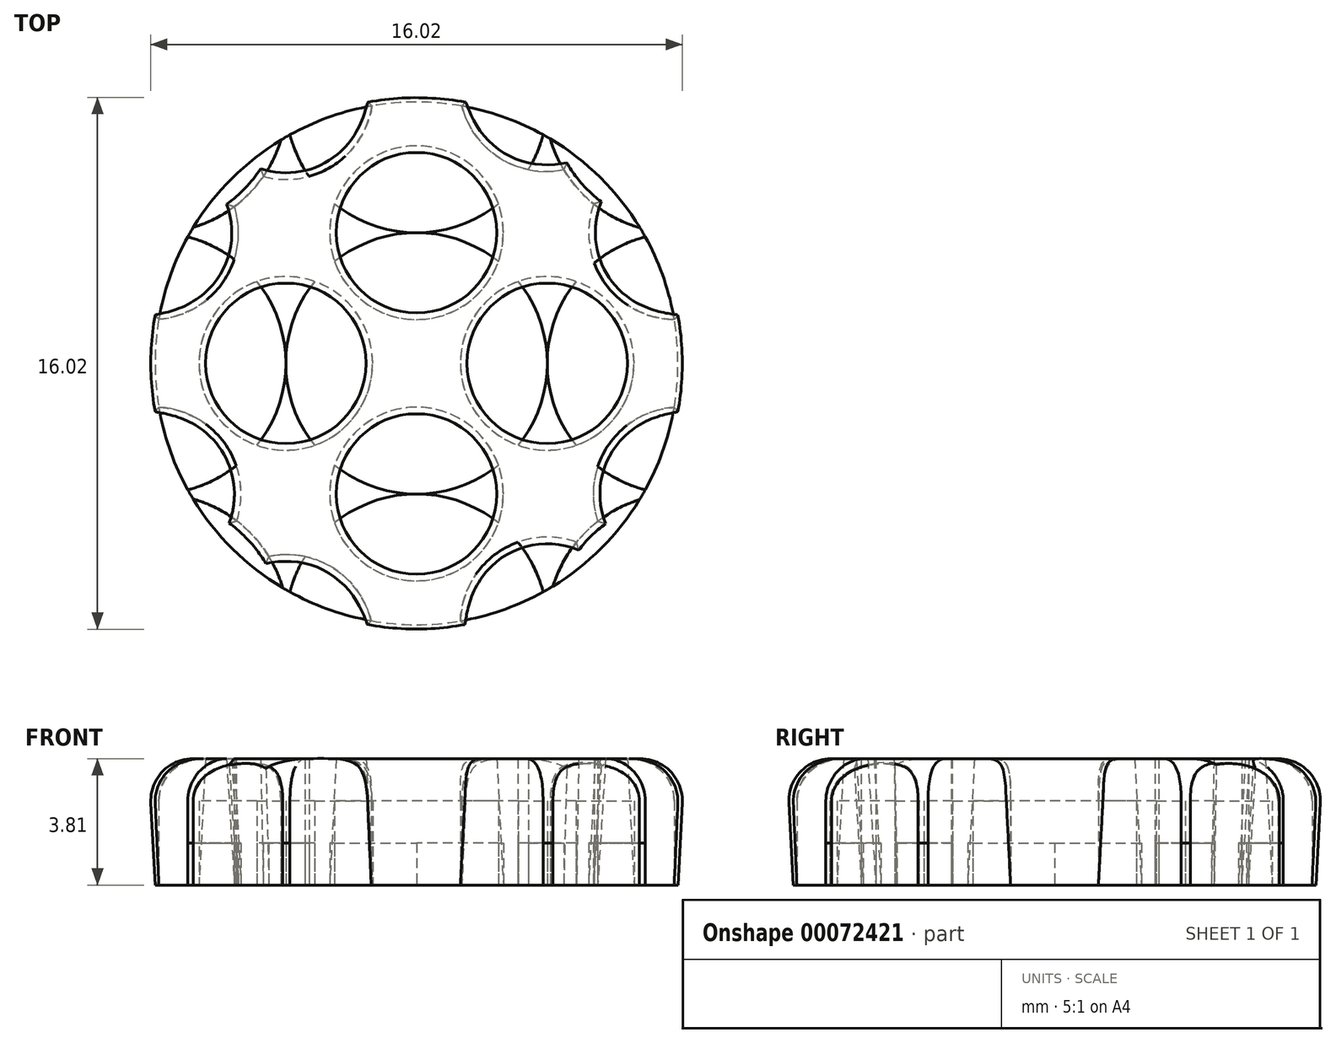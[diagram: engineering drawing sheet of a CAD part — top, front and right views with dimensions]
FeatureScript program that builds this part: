
annotation { "Feature Type Name" : "Feature", "Feature Type Description" : "" }
export const myFeature = defineFeature(function(context is Context, id is Id, definition is map)
    precondition{}
    {
        {
            var Q0;
            Q0=qCreatedBy(makeId("Top.planeOp"),FACE);
            var sketch = newSketch(context, id + "F0", { "sketchPlane" : qUnion([Q0])});
            skCircle(sketch, "E0", {"center": v(0, 0) * mm, "radius": 7.87 * mm});
            skCircle(sketch, "E1", {"center": v(0, 0) * mm, "radius": 3.94 * mm});
            skCircle(sketch, "E2", {"center": v(3.94, 0) * mm, "radius": 2.62 * mm});
            skCircle(sketch, "E3", {"center": v(-3.94, 0) * mm, "radius": 2.62 * mm});
            skCircle(sketch, "E4", {"center": v(0, 3.94) * mm, "radius": 2.62 * mm});
            skCircle(sketch, "E5", {"center": v(0, -3.94) * mm, "radius": 2.62 * mm});
            skCircle(sketch, "E6", {"center": v(-7.87, 0) * mm, "radius": 3.94 * mm});
            skCircle(sketch, "E7", {"center": v(7.87, 0) * mm, "radius": 3.94 * mm});
            skCircle(sketch, "E8", {"center": v(0, 7.87) * mm, "radius": 3.94 * mm});
            skCircle(sketch, "E9", {"center": v(0, -7.87) * mm, "radius": 3.94 * mm});
            skCircle(sketch, "E10", {"center": v(-7.85, 7.87) * mm, "radius": 3.94 * mm});
            skPoint(sketch, "E10.first.point", {"position": v(-3.93, 8.16) * mm});
            skPoint(sketch, "E10.second.point", {"position": v(-11.67, 8.83) * mm});
            skPoint(sketch, "E10.third.point", {"position": v(-7.98, 3.94) * mm});
            skCircle(sketch, "E11", {"center": v(7.8, 7.87) * mm, "radius": 3.94 * mm});
            skPoint(sketch, "E11.first.point", {"position": v(3.9, 8.4) * mm});
            skPoint(sketch, "E11.second.point", {"position": v(11.72, 8.27) * mm});
            skPoint(sketch, "E11.third.point", {"position": v(7.8, 3.94) * mm});
            skCircle(sketch, "E12", {"center": v(7.87, -7.87) * mm, "radius": 3.94 * mm});
            skPoint(sketch, "E12.first.point", {"position": v(7.94, -3.94) * mm});
            skPoint(sketch, "E12.second.point", {"position": v(7.53, -11.8) * mm});
            skPoint(sketch, "E12.third.point", {"position": v(3.94, -7.85) * mm});
            skCircle(sketch, "E13", {"center": v(-7.8, -7.87) * mm, "radius": 3.94 * mm});
            skPoint(sketch, "E13.first.point", {"position": v(-7.9, -3.94) * mm});
            skPoint(sketch, "E13.second.point", {"position": v(-9.84, -11.24) * mm});
            skPoint(sketch, "E13.third.point", {"position": v(-3.9, -8.38) * mm});
            skCircle(sketch, "E14", {"center": v(-3.9, -8.38) * mm, "radius": 2.62 * mm});
            skCircle(sketch, "E15", {"center": v(3.94, -7.85) * mm, "radius": 2.62 * mm});
            skCircle(sketch, "E16", {"center": v(7.8, 3.94) * mm, "radius": 2.62 * mm});
            skCircle(sketch, "E17", {"center": v(7.94, -3.94) * mm, "radius": 2.62 * mm});
            skCircle(sketch, "E18", {"center": v(-7.9, -3.94) * mm, "radius": 2.62 * mm});
            skCircle(sketch, "E19", {"center": v(3.9, 8.4) * mm, "radius": 2.62 * mm});
            skCircle(sketch, "E20", {"center": v(-7.98, 3.94) * mm, "radius": 2.62 * mm});
            skCircle(sketch, "E21", {"center": v(-3.93, 8.16) * mm, "radius": 2.62 * mm});
            skSolve(sketch);
        }
        {
            var Q0;
            {var subQ0=sQuery(id+"F0.wireOp",EDGE,"E13");var subQ1=sQuery(id+"F0.wireOp",EDGE,"E0");var subQ2=makeQuery(id+"F0.imprint","INTERSECT",VERTEX,{"disambiguationData":[OD(1.0)],"derivedFrom":[subQ1,subQ0]});Q0=makeQuery(id+"F0.imprint","IMPRINT",FACE,{"disambiguationData":[TD([[makeQuery(id+"F0.imprint","IMPRINT",EDGE,{"disambiguationData":[TD([[subQ2,-1.0]])],"derivedFrom":subQ1}),1.0]])]});}
            var Q1;
            {var subQ0=sQuery(id+"F0.wireOp",EDGE,"E8");var subQ1=sQuery(id+"F0.wireOp",EDGE,"E1");var subQ2=makeQuery(id+"F0.imprint","INTERSECT",VERTEX,{"derivedFrom":[subQ1,subQ0]});Q1=makeQuery(id+"F0.imprint","IMPRINT",FACE,{"disambiguationData":[TD([[makeQuery(id+"F0.imprint","IMPRINT",EDGE,{"disambiguationData":[TD([[subQ2,-1.0]])],"derivedFrom":subQ1}),-1.0]])]});}
            var Q2;
            {var subQ0=sQuery(id+"F0.wireOp",EDGE,"E8");var subQ1=sQuery(id+"F0.wireOp",EDGE,"E0");var subQ2=makeQuery(id+"F0.imprint","INTERSECT",VERTEX,{"disambiguationData":[OD(1.0)],"derivedFrom":[subQ1,subQ0]});Q2=makeQuery(id+"F0.imprint","IMPRINT",FACE,{"disambiguationData":[TD([[makeQuery(id+"F0.imprint","IMPRINT",EDGE,{"disambiguationData":[TD([[subQ2,-1.0]])],"derivedFrom":subQ1}),1.0]])]});}
            var Q3;
            {var subQ0=sQuery(id+"F0.wireOp",EDGE,"E10");var subQ1=sQuery(id+"F0.wireOp",EDGE,"E0");var subQ2=makeQuery(id+"F0.imprint","INTERSECT",VERTEX,{"disambiguationData":[OD(1.0)],"derivedFrom":[subQ1,subQ0]});Q3=makeQuery(id+"F0.imprint","IMPRINT",FACE,{"disambiguationData":[TD([[makeQuery(id+"F0.imprint","IMPRINT",EDGE,{"disambiguationData":[TD([[subQ2,-1.0]])],"derivedFrom":subQ1}),1.0]])]});}
            var Q4;
            {var subQ0=sQuery(id+"F0.wireOp",EDGE,"E2");var subQ1=sQuery(id+"F0.wireOp",EDGE,"E1");var subQ2=makeQuery(id+"F0.imprint","INTERSECT",VERTEX,{"disambiguationData":[OD(0.0)],"derivedFrom":[subQ1,subQ0]});Q4=makeQuery(id+"F0.imprint","IMPRINT",FACE,{"disambiguationData":[TD([[makeQuery(id+"F0.imprint","IMPRINT",EDGE,{"disambiguationData":[TD([[subQ2,1.0]])],"derivedFrom":subQ1}),-1.0]])]});}
            var Q5;
            {var subQ0=sQuery(id+"F0.wireOp",EDGE,"E4");var subQ1=sQuery(id+"F0.wireOp",EDGE,"E1");var subQ2=makeQuery(id+"F0.imprint","INTERSECT",VERTEX,{"disambiguationData":[OD(0.0)],"derivedFrom":[subQ1,subQ0]});Q5=makeQuery(id+"F0.imprint","IMPRINT",FACE,{"disambiguationData":[TD([[makeQuery(id+"F0.imprint","IMPRINT",EDGE,{"disambiguationData":[TD([[subQ2,-1.0]])],"derivedFrom":subQ1}),-1.0]])]});}
            var Q6;
            {var subQ0=sQuery(id+"F0.wireOp",EDGE,"E7");var subQ1=sQuery(id+"F0.wireOp",EDGE,"E1");var subQ2=makeQuery(id+"F0.imprint","INTERSECT",VERTEX,{"derivedFrom":[subQ1,subQ0]});Q6=makeQuery(id+"F0.imprint","IMPRINT",FACE,{"disambiguationData":[TD([[makeQuery(id+"F0.imprint","IMPRINT",EDGE,{"disambiguationData":[TD([[subQ2,1.0]])],"derivedFrom":subQ1}),-1.0]])]});}
            var Q7;
            {var subQ0=sQuery(id+"F0.wireOp",EDGE,"E6");var subQ1=sQuery(id+"F0.wireOp",EDGE,"E0");var subQ2=makeQuery(id+"F0.imprint","INTERSECT",VERTEX,{"disambiguationData":[OD(1.0)],"derivedFrom":[subQ1,subQ0]});Q7=makeQuery(id+"F0.imprint","IMPRINT",FACE,{"disambiguationData":[TD([[makeQuery(id+"F0.imprint","IMPRINT",EDGE,{"disambiguationData":[TD([[subQ2,-1.0]])],"derivedFrom":subQ1}),1.0]])]});}
            var Q8;
            {var subQ0=sQuery(id+"F0.wireOp",EDGE,"E6");var subQ1=sQuery(id+"F0.wireOp",EDGE,"E1");var subQ2=makeQuery(id+"F0.imprint","INTERSECT",VERTEX,{"derivedFrom":[subQ1,subQ0]});Q8=makeQuery(id+"F0.imprint","IMPRINT",FACE,{"disambiguationData":[TD([[makeQuery(id+"F0.imprint","IMPRINT",EDGE,{"disambiguationData":[TD([[subQ2,-1.0]])],"derivedFrom":subQ1}),-1.0]])]});}
            var Q9;
            {var subQ0=sQuery(id+"F0.wireOp",EDGE,"E7");var subQ1=sQuery(id+"F0.wireOp",EDGE,"E0");var subQ2=makeQuery(id+"F0.imprint","INTERSECT",VERTEX,{"disambiguationData":[OD(0.0)],"derivedFrom":[subQ1,subQ0]});Q9=makeQuery(id+"F0.imprint","IMPRINT",FACE,{"disambiguationData":[TD([[makeQuery(id+"F0.imprint","IMPRINT",EDGE,{"disambiguationData":[TD([[subQ2,-1.0]])],"derivedFrom":subQ1}),1.0]])]});}
            var Q10;
            {var subQ0=sQuery(id+"F0.wireOp",EDGE,"E5");var subQ1=sQuery(id+"F0.wireOp",EDGE,"E1");var subQ2=makeQuery(id+"F0.imprint","INTERSECT",VERTEX,{"disambiguationData":[OD(0.0)],"derivedFrom":[subQ1,subQ0]});Q10=makeQuery(id+"F0.imprint","IMPRINT",FACE,{"disambiguationData":[TD([[makeQuery(id+"F0.imprint","IMPRINT",EDGE,{"disambiguationData":[TD([[subQ2,-1.0]])],"derivedFrom":subQ1}),-1.0]])]});}
            var Q11;
            {var subQ0=sQuery(id+"F0.wireOp",EDGE,"E12");var subQ1=sQuery(id+"F0.wireOp",EDGE,"E0");var subQ2=makeQuery(id+"F0.imprint","INTERSECT",VERTEX,{"disambiguationData":[OD(1.0)],"derivedFrom":[subQ1,subQ0]});Q11=makeQuery(id+"F0.imprint","IMPRINT",FACE,{"disambiguationData":[TD([[makeQuery(id+"F0.imprint","IMPRINT",EDGE,{"disambiguationData":[TD([[subQ2,-1.0]])],"derivedFrom":subQ1}),1.0]])]});}
            var Q12;
            {var subQ0=sQuery(id+"F0.wireOp",EDGE,"E3");var subQ1=sQuery(id+"F0.wireOp",EDGE,"E1");var subQ2=makeQuery(id+"F0.imprint","INTERSECT",VERTEX,{"disambiguationData":[OD(0.0)],"derivedFrom":[subQ1,subQ0]});Q12=makeQuery(id+"F0.imprint","IMPRINT",FACE,{"disambiguationData":[TD([[makeQuery(id+"F0.imprint","IMPRINT",EDGE,{"disambiguationData":[TD([[subQ2,-1.0]])],"derivedFrom":subQ1}),-1.0]])]});}
            var Q13;
            {var subQ0=sQuery(id+"F0.wireOp",EDGE,"E11");var subQ1=sQuery(id+"F0.wireOp",EDGE,"E0");var subQ2=makeQuery(id+"F0.imprint","INTERSECT",VERTEX,{"disambiguationData":[OD(1.0)],"derivedFrom":[subQ1,subQ0]});Q13=makeQuery(id+"F0.imprint","IMPRINT",FACE,{"disambiguationData":[TD([[makeQuery(id+"F0.imprint","IMPRINT",EDGE,{"disambiguationData":[TD([[subQ2,-1.0]])],"derivedFrom":subQ1}),1.0]])]});}
            var Q14;
            {var subQ0=sQuery(id+"F0.wireOp",EDGE,"E9");var subQ1=sQuery(id+"F0.wireOp",EDGE,"E1");var subQ2=makeQuery(id+"F0.imprint","INTERSECT",VERTEX,{"derivedFrom":[subQ1,subQ0]});Q14=makeQuery(id+"F0.imprint","IMPRINT",FACE,{"disambiguationData":[TD([[makeQuery(id+"F0.imprint","IMPRINT",EDGE,{"disambiguationData":[TD([[subQ2,-1.0]])],"derivedFrom":subQ1}),-1.0]])]});}
            var Q15;
            {var subQ0=sQuery(id+"F0.wireOp",EDGE,"E9");var subQ1=sQuery(id+"F0.wireOp",EDGE,"E0");var subQ2=makeQuery(id+"F0.imprint","INTERSECT",VERTEX,{"disambiguationData":[OD(1.0)],"derivedFrom":[subQ1,subQ0]});Q15=makeQuery(id+"F0.imprint","IMPRINT",FACE,{"disambiguationData":[TD([[makeQuery(id+"F0.imprint","IMPRINT",EDGE,{"disambiguationData":[TD([[subQ2,-1.0]])],"derivedFrom":subQ1}),1.0]])]});}
            extrude(context, id + "F1", {"entities" : qUnion([Q0, Q1, Q2, Q3, Q4, Q5, Q6, Q7, Q8, Q9, Q10, Q11, Q12, Q13, Q14, Q15]), "depth" : 1.27 * mm});
        }
        {
            var Q0;
            {var subQ9=sQuery(id+"F0.wireOp",EDGE,"E1");var subQ11=sQuery(id+"F0.wireOp",EDGE,"E5");var subQ12=makeQuery(id+"F0.imprint","INTERSECT",VERTEX,{"disambiguationData":[OD(1.0)],"derivedFrom":[subQ9,subQ11]});Q0=makeQuery(id+"F0.imprint","IMPRINT",FACE,{"disambiguationData":[TD([[makeQuery(id+"F0.imprint","IMPRINT",EDGE,{"disambiguationData":[TD([[subQ12,-1.0]])],"derivedFrom":subQ9}),-1.0]])]});}
            var Q1;
            {var subQ3=sQuery(id+"F0.wireOp",EDGE,"E19");var subQ8=sQuery(id+"F0.wireOp",EDGE,"E0");var subQ9=makeQuery(id+"F0.imprint","INTERSECT",VERTEX,{"disambiguationData":[OD(1.0)],"derivedFrom":[subQ8,subQ3]});Q1=makeQuery(id+"F0.imprint","IMPRINT",FACE,{"disambiguationData":[TD([[makeQuery(id+"F0.imprint","IMPRINT",EDGE,{"disambiguationData":[TD([[subQ9,-1.0]])],"derivedFrom":subQ8}),1.0]])]});}
            var Q2;
            {var subQ3=sQuery(id+"F0.wireOp",EDGE,"E14");var subQ6=sQuery(id+"F0.wireOp",EDGE,"E0");var subQ10=makeQuery(id+"F0.imprint","INTERSECT",VERTEX,{"disambiguationData":[OD(1.0)],"derivedFrom":[subQ6,subQ3]});Q2=makeQuery(id+"F0.imprint","IMPRINT",FACE,{"disambiguationData":[TD([[makeQuery(id+"F0.imprint","IMPRINT",EDGE,{"disambiguationData":[TD([[subQ10,-1.0]])],"derivedFrom":subQ6}),1.0]])]});}
            var Q3;
            {var subQ1=sQuery(id+"F0.wireOp",EDGE,"E1");var subQ5=sQuery(id+"F0.wireOp",EDGE,"E3");var subQ6=makeQuery(id+"F0.imprint","INTERSECT",VERTEX,{"disambiguationData":[OD(1.0)],"derivedFrom":[subQ1,subQ5]});Q3=makeQuery(id+"F0.imprint","IMPRINT",FACE,{"disambiguationData":[TD([[makeQuery(id+"F0.imprint","IMPRINT",EDGE,{"disambiguationData":[TD([[subQ6,-1.0]])],"derivedFrom":subQ1}),-1.0]])]});}
            var Q4;
            {var subQ6=sQuery(id+"F0.wireOp",EDGE,"E20");var subQ7=sQuery(id+"F0.wireOp",EDGE,"E0");var subQ8=makeQuery(id+"F0.imprint","INTERSECT",VERTEX,{"disambiguationData":[OD(1.0)],"derivedFrom":[subQ7,subQ6]});Q4=makeQuery(id+"F0.imprint","IMPRINT",FACE,{"disambiguationData":[TD([[makeQuery(id+"F0.imprint","IMPRINT",EDGE,{"disambiguationData":[TD([[subQ8,-1.0]])],"derivedFrom":subQ7}),1.0]])]});}
            var Q5;
            {var subQ1=sQuery(id+"F0.wireOp",EDGE,"E1");var subQ3=sQuery(id+"F0.wireOp",EDGE,"E2");var subQ11=makeQuery(id+"F0.imprint","INTERSECT",VERTEX,{"disambiguationData":[OD(0.0)],"derivedFrom":[subQ1,subQ3]});Q5=makeQuery(id+"F0.imprint","IMPRINT",FACE,{"disambiguationData":[TD([[makeQuery(id+"F0.imprint","IMPRINT",EDGE,{"disambiguationData":[TD([[subQ11,-1.0]])],"derivedFrom":subQ1}),1.0]])]});}
            var Q6;
            {var subQ6=sQuery(id+"F0.wireOp",EDGE,"E16");var subQ8=sQuery(id+"F0.wireOp",EDGE,"E0");var subQ9=makeQuery(id+"F0.imprint","INTERSECT",VERTEX,{"disambiguationData":[OD(0.0)],"derivedFrom":[subQ8,subQ6]});Q6=makeQuery(id+"F0.imprint","IMPRINT",FACE,{"disambiguationData":[TD([[makeQuery(id+"F0.imprint","IMPRINT",EDGE,{"disambiguationData":[TD([[subQ9,1.0]])],"derivedFrom":subQ8}),1.0]])]});}
            var Q7;
            {var subQ5=sQuery(id+"F0.wireOp",EDGE,"E4");var subQ6=sQuery(id+"F0.wireOp",EDGE,"E1");var subQ7=makeQuery(id+"F0.imprint","INTERSECT",VERTEX,{"disambiguationData":[OD(1.0)],"derivedFrom":[subQ6,subQ5]});Q7=makeQuery(id+"F0.imprint","IMPRINT",FACE,{"disambiguationData":[TD([[makeQuery(id+"F0.imprint","IMPRINT",EDGE,{"disambiguationData":[TD([[subQ7,-1.0]])],"derivedFrom":subQ6}),-1.0]])]});}
            var Q8;
            {var subQ1=sQuery(id+"F0.wireOp",EDGE,"E2");var subQ5=sQuery(id+"F0.wireOp",EDGE,"E1");var subQ6=makeQuery(id+"F0.imprint","INTERSECT",VERTEX,{"disambiguationData":[OD(0.0)],"derivedFrom":[subQ5,subQ1]});Q8=makeQuery(id+"F0.imprint","IMPRINT",FACE,{"disambiguationData":[TD([[makeQuery(id+"F0.imprint","IMPRINT",EDGE,{"disambiguationData":[TD([[subQ6,-1.0]])],"derivedFrom":subQ5}),-1.0]])]});}
            extrude(context, id + "F2", {"entities" : qUnion([Q0, Q1, Q2, Q3, Q4, Q5, Q6, Q7, Q8]), "depth" : 3.8 * mm, "hasDraft" : true, "draftAngle" : 3 * degree});
        }
        {
            var Q0;
            {var subQ0=sQuery(id+"F0.wireOp",EDGE,"E2");var subQ1=sQuery(id+"F0.wireOp",EDGE,"E1");var subQ2=makeQuery(id+"F0.imprint","INTERSECT",VERTEX,{"disambiguationData":[OD(0.0)],"derivedFrom":[subQ1,subQ0]});Q0=makeQuery(id+"F0.imprint","IMPRINT",FACE,{"disambiguationData":[TD([[makeQuery(id+"F0.imprint","IMPRINT",EDGE,{"disambiguationData":[TD([[subQ2,1.0]])],"derivedFrom":subQ1}),1.0]])]});}
            var Q1;
            {var subQ0=sQuery(id+"F0.wireOp",EDGE,"E5");var subQ1=sQuery(id+"F0.wireOp",EDGE,"E1");var subQ2=makeQuery(id+"F0.imprint","INTERSECT",VERTEX,{"disambiguationData":[OD(0.0)],"derivedFrom":[subQ1,subQ0]});Q1=makeQuery(id+"F0.imprint","IMPRINT",FACE,{"disambiguationData":[TD([[makeQuery(id+"F0.imprint","IMPRINT",EDGE,{"disambiguationData":[TD([[subQ2,-1.0]])],"derivedFrom":subQ1}),1.0]])]});}
            var Q2;
            {var subQ0=sQuery(id+"F0.wireOp",EDGE,"E4");var subQ1=sQuery(id+"F0.wireOp",EDGE,"E1");var subQ2=makeQuery(id+"F0.imprint","INTERSECT",VERTEX,{"disambiguationData":[OD(0.0)],"derivedFrom":[subQ1,subQ0]});Q2=makeQuery(id+"F0.imprint","IMPRINT",FACE,{"disambiguationData":[TD([[makeQuery(id+"F0.imprint","IMPRINT",EDGE,{"disambiguationData":[TD([[subQ2,-1.0]])],"derivedFrom":subQ1}),1.0]])]});}
            var Q3;
            {var subQ0=sQuery(id+"F0.wireOp",EDGE,"E8");var subQ1=sQuery(id+"F0.wireOp",EDGE,"E4");var subQ2=makeQuery(id+"F0.imprint","INTERSECT",VERTEX,{"disambiguationData":[OD(0.0)],"derivedFrom":[subQ1,subQ0]});Q3=makeQuery(id+"F0.imprint","IMPRINT",FACE,{"disambiguationData":[TD([[makeQuery(id+"F0.imprint","IMPRINT",EDGE,{"disambiguationData":[TD([[subQ2,1.0]])],"derivedFrom":subQ1}),1.0]])]});}
            var Q4;
            {var subQ0=sQuery(id+"F0.wireOp",EDGE,"E6");var subQ1=sQuery(id+"F0.wireOp",EDGE,"E3");var subQ2=makeQuery(id+"F0.imprint","INTERSECT",VERTEX,{"disambiguationData":[OD(0.0)],"derivedFrom":[subQ1,subQ0]});Q4=makeQuery(id+"F0.imprint","IMPRINT",FACE,{"disambiguationData":[TD([[makeQuery(id+"F0.imprint","IMPRINT",EDGE,{"disambiguationData":[TD([[subQ2,-1.0]])],"derivedFrom":subQ1}),1.0]])]});}
            var Q5;
            {var subQ0=sQuery(id+"F0.wireOp",EDGE,"E7");var subQ1=sQuery(id+"F0.wireOp",EDGE,"E2");var subQ2=makeQuery(id+"F0.imprint","INTERSECT",VERTEX,{"disambiguationData":[OD(0.0)],"derivedFrom":[subQ1,subQ0]});Q5=makeQuery(id+"F0.imprint","IMPRINT",FACE,{"disambiguationData":[TD([[makeQuery(id+"F0.imprint","IMPRINT",EDGE,{"disambiguationData":[TD([[subQ2,1.0]])],"derivedFrom":subQ1}),1.0]])]});}
            var Q6;
            {var subQ0=sQuery(id+"F0.wireOp",EDGE,"E9");var subQ1=sQuery(id+"F0.wireOp",EDGE,"E5");var subQ2=makeQuery(id+"F0.imprint","INTERSECT",VERTEX,{"disambiguationData":[OD(0.0)],"derivedFrom":[subQ1,subQ0]});Q6=makeQuery(id+"F0.imprint","IMPRINT",FACE,{"disambiguationData":[TD([[makeQuery(id+"F0.imprint","IMPRINT",EDGE,{"disambiguationData":[TD([[subQ2,-1.0]])],"derivedFrom":subQ1}),1.0]])]});}
            var Q7;
            {var subQ0=sQuery(id+"F0.wireOp",EDGE,"E3");var subQ1=sQuery(id+"F0.wireOp",EDGE,"E1");var subQ2=makeQuery(id+"F0.imprint","INTERSECT",VERTEX,{"disambiguationData":[OD(0.0)],"derivedFrom":[subQ1,subQ0]});Q7=makeQuery(id+"F0.imprint","IMPRINT",FACE,{"disambiguationData":[TD([[makeQuery(id+"F0.imprint","IMPRINT",EDGE,{"disambiguationData":[TD([[subQ2,-1.0]])],"derivedFrom":subQ1}),1.0]])]});}
            extrude(context, id + "F3", {"entities" : qUnion([Q0, Q1, Q2, Q3, Q4, Q5, Q6, Q7]), "depth" : 2.54 * mm});
        }
        {
            var Q0;
            {var subQ0=sQuery(id+"F0.wireOp",EDGE,"E7");var subQ1=sQuery(id+"F0.wireOp",EDGE,"E0");var subQ2=makeQuery(id+"F0.imprint","INTERSECT",VERTEX,{"disambiguationData":[OD(0.0)],"derivedFrom":[subQ1,subQ0]});Q0=makeQuery(id+"F0.imprint","IMPRINT",FACE,{"disambiguationData":[TD([[makeQuery(id+"F0.imprint","IMPRINT",EDGE,{"disambiguationData":[TD([[subQ2,1.0]])],"derivedFrom":subQ1}),1.0]])]});}
            var Q1;
            {var subQ0=sQuery(id+"F0.wireOp",EDGE,"E9");var subQ1=sQuery(id+"F0.wireOp",EDGE,"E0");var subQ2=makeQuery(id+"F0.imprint","INTERSECT",VERTEX,{"disambiguationData":[OD(0.0)],"derivedFrom":[subQ1,subQ0]});Q1=makeQuery(id+"F0.imprint","IMPRINT",FACE,{"disambiguationData":[TD([[makeQuery(id+"F0.imprint","IMPRINT",EDGE,{"disambiguationData":[TD([[subQ2,-1.0]])],"derivedFrom":subQ1}),1.0]])]});}
            var Q2;
            {var subQ0=sQuery(id+"F0.wireOp",EDGE,"E18");var subQ1=sQuery(id+"F0.wireOp",EDGE,"E0");var subQ2=makeQuery(id+"F0.imprint","INTERSECT",VERTEX,{"disambiguationData":[OD(0.0)],"derivedFrom":[subQ1,subQ0]});Q2=makeQuery(id+"F0.imprint","IMPRINT",FACE,{"disambiguationData":[TD([[makeQuery(id+"F0.imprint","IMPRINT",EDGE,{"disambiguationData":[TD([[subQ2,-1.0]])],"derivedFrom":subQ1}),1.0]])]});}
            var Q3;
            {var subQ0=sQuery(id+"F0.wireOp",EDGE,"E10");var subQ1=sQuery(id+"F0.wireOp",EDGE,"E0");var subQ2=makeQuery(id+"F0.imprint","INTERSECT",VERTEX,{"disambiguationData":[OD(0.0)],"derivedFrom":[subQ1,subQ0]});Q3=makeQuery(id+"F0.imprint","IMPRINT",FACE,{"disambiguationData":[TD([[makeQuery(id+"F0.imprint","IMPRINT",EDGE,{"disambiguationData":[TD([[subQ2,-1.0]])],"derivedFrom":subQ1}),1.0]])]});}
            var Q4;
            {var subQ0=sQuery(id+"F0.wireOp",EDGE,"E13");var subQ1=sQuery(id+"F0.wireOp",EDGE,"E0");var subQ2=makeQuery(id+"F0.imprint","INTERSECT",VERTEX,{"disambiguationData":[OD(0.0)],"derivedFrom":[subQ1,subQ0]});Q4=makeQuery(id+"F0.imprint","IMPRINT",FACE,{"disambiguationData":[TD([[makeQuery(id+"F0.imprint","IMPRINT",EDGE,{"disambiguationData":[TD([[subQ2,-1.0]])],"derivedFrom":subQ1}),1.0]])]});}
            var Q5;
            {var subQ0=sQuery(id+"F0.wireOp",EDGE,"E14");var subQ1=sQuery(id+"F0.wireOp",EDGE,"E0");var subQ2=makeQuery(id+"F0.imprint","INTERSECT",VERTEX,{"disambiguationData":[OD(0.0)],"derivedFrom":[subQ1,subQ0]});Q5=makeQuery(id+"F0.imprint","IMPRINT",FACE,{"disambiguationData":[TD([[makeQuery(id+"F0.imprint","IMPRINT",EDGE,{"disambiguationData":[TD([[subQ2,-1.0]])],"derivedFrom":subQ1}),1.0]])]});}
            var Q6;
            {var subQ0=sQuery(id+"F0.wireOp",EDGE,"E15");var subQ1=sQuery(id+"F0.wireOp",EDGE,"E0");var subQ2=makeQuery(id+"F0.imprint","INTERSECT",VERTEX,{"disambiguationData":[OD(0.0)],"derivedFrom":[subQ1,subQ0]});Q6=makeQuery(id+"F0.imprint","IMPRINT",FACE,{"disambiguationData":[TD([[makeQuery(id+"F0.imprint","IMPRINT",EDGE,{"disambiguationData":[TD([[subQ2,-1.0]])],"derivedFrom":subQ1}),1.0]])]});}
            var Q7;
            {var subQ0=sQuery(id+"F0.wireOp",EDGE,"E16");var subQ1=sQuery(id+"F0.wireOp",EDGE,"E0");var subQ2=makeQuery(id+"F0.imprint","INTERSECT",VERTEX,{"disambiguationData":[OD(1.0)],"derivedFrom":[subQ1,subQ0]});Q7=makeQuery(id+"F0.imprint","IMPRINT",FACE,{"disambiguationData":[TD([[makeQuery(id+"F0.imprint","IMPRINT",EDGE,{"disambiguationData":[TD([[subQ2,-1.0]])],"derivedFrom":subQ1}),1.0]])]});}
            var Q8;
            {var subQ0=sQuery(id+"F0.wireOp",EDGE,"E12");var subQ1=sQuery(id+"F0.wireOp",EDGE,"E0");var subQ2=makeQuery(id+"F0.imprint","INTERSECT",VERTEX,{"disambiguationData":[OD(0.0)],"derivedFrom":[subQ1,subQ0]});Q8=makeQuery(id+"F0.imprint","IMPRINT",FACE,{"disambiguationData":[TD([[makeQuery(id+"F0.imprint","IMPRINT",EDGE,{"disambiguationData":[TD([[subQ2,-1.0]])],"derivedFrom":subQ1}),1.0]])]});}
            var Q9;
            {var subQ0=sQuery(id+"F0.wireOp",EDGE,"E15");var subQ1=sQuery(id+"F0.wireOp",EDGE,"E0");var subQ2=makeQuery(id+"F0.imprint","INTERSECT",VERTEX,{"disambiguationData":[OD(1.0)],"derivedFrom":[subQ1,subQ0]});Q9=makeQuery(id+"F0.imprint","IMPRINT",FACE,{"disambiguationData":[TD([[makeQuery(id+"F0.imprint","IMPRINT",EDGE,{"disambiguationData":[TD([[subQ2,-1.0]])],"derivedFrom":subQ1}),1.0]])]});}
            var Q10;
            {var subQ0=sQuery(id+"F0.wireOp",EDGE,"E7");var subQ1=sQuery(id+"F0.wireOp",EDGE,"E0");var subQ2=makeQuery(id+"F0.imprint","INTERSECT",VERTEX,{"disambiguationData":[OD(1.0)],"derivedFrom":[subQ1,subQ0]});Q10=makeQuery(id+"F0.imprint","IMPRINT",FACE,{"disambiguationData":[TD([[makeQuery(id+"F0.imprint","IMPRINT",EDGE,{"disambiguationData":[TD([[subQ2,-1.0]])],"derivedFrom":subQ1}),1.0]])]});}
            var Q11;
            {var subQ0=sQuery(id+"F0.wireOp",EDGE,"E11");var subQ1=sQuery(id+"F0.wireOp",EDGE,"E0");var subQ2=makeQuery(id+"F0.imprint","INTERSECT",VERTEX,{"disambiguationData":[OD(0.0)],"derivedFrom":[subQ1,subQ0]});Q11=makeQuery(id+"F0.imprint","IMPRINT",FACE,{"disambiguationData":[TD([[makeQuery(id+"F0.imprint","IMPRINT",EDGE,{"disambiguationData":[TD([[subQ2,-1.0]])],"derivedFrom":subQ1}),1.0]])]});}
            var Q12;
            {var subQ0=sQuery(id+"F0.wireOp",EDGE,"E8");var subQ1=sQuery(id+"F0.wireOp",EDGE,"E0");var subQ2=makeQuery(id+"F0.imprint","INTERSECT",VERTEX,{"disambiguationData":[OD(0.0)],"derivedFrom":[subQ1,subQ0]});Q12=makeQuery(id+"F0.imprint","IMPRINT",FACE,{"disambiguationData":[TD([[makeQuery(id+"F0.imprint","IMPRINT",EDGE,{"disambiguationData":[TD([[subQ2,-1.0]])],"derivedFrom":subQ1}),1.0]])]});}
            var Q13;
            {var subQ0=sQuery(id+"F0.wireOp",EDGE,"E20");var subQ1=sQuery(id+"F0.wireOp",EDGE,"E0");var subQ2=makeQuery(id+"F0.imprint","INTERSECT",VERTEX,{"disambiguationData":[OD(0.0)],"derivedFrom":[subQ1,subQ0]});Q13=makeQuery(id+"F0.imprint","IMPRINT",FACE,{"disambiguationData":[TD([[makeQuery(id+"F0.imprint","IMPRINT",EDGE,{"disambiguationData":[TD([[subQ2,-1.0]])],"derivedFrom":subQ1}),1.0]])]});}
            var Q14;
            {var subQ0=sQuery(id+"F0.wireOp",EDGE,"E21");var subQ1=sQuery(id+"F0.wireOp",EDGE,"E0");var subQ2=makeQuery(id+"F0.imprint","INTERSECT",VERTEX,{"disambiguationData":[OD(1.0)],"derivedFrom":[subQ1,subQ0]});Q14=makeQuery(id+"F0.imprint","IMPRINT",FACE,{"disambiguationData":[TD([[makeQuery(id+"F0.imprint","IMPRINT",EDGE,{"disambiguationData":[TD([[subQ2,-1.0]])],"derivedFrom":subQ1}),1.0]])]});}
            var Q15;
            {var subQ0=sQuery(id+"F0.wireOp",EDGE,"E21");var subQ1=sQuery(id+"F0.wireOp",EDGE,"E0");var subQ2=makeQuery(id+"F0.imprint","INTERSECT",VERTEX,{"disambiguationData":[OD(0.0)],"derivedFrom":[subQ1,subQ0]});Q15=makeQuery(id+"F0.imprint","IMPRINT",FACE,{"disambiguationData":[TD([[makeQuery(id+"F0.imprint","IMPRINT",EDGE,{"disambiguationData":[TD([[subQ2,-1.0]])],"derivedFrom":subQ1}),1.0]])]});}
            var Q16;
            {var subQ0=sQuery(id+"F0.wireOp",EDGE,"E19");var subQ1=sQuery(id+"F0.wireOp",EDGE,"E0");var subQ2=makeQuery(id+"F0.imprint","INTERSECT",VERTEX,{"disambiguationData":[OD(0.0)],"derivedFrom":[subQ1,subQ0]});Q16=makeQuery(id+"F0.imprint","IMPRINT",FACE,{"disambiguationData":[TD([[makeQuery(id+"F0.imprint","IMPRINT",EDGE,{"disambiguationData":[TD([[subQ2,-1.0]])],"derivedFrom":subQ1}),1.0]])]});}
            var Q17;
            {var subQ0=sQuery(id+"F0.wireOp",EDGE,"E18");var subQ1=sQuery(id+"F0.wireOp",EDGE,"E0");var subQ2=makeQuery(id+"F0.imprint","INTERSECT",VERTEX,{"disambiguationData":[OD(1.0)],"derivedFrom":[subQ1,subQ0]});Q17=makeQuery(id+"F0.imprint","IMPRINT",FACE,{"disambiguationData":[TD([[makeQuery(id+"F0.imprint","IMPRINT",EDGE,{"disambiguationData":[TD([[subQ2,-1.0]])],"derivedFrom":subQ1}),1.0]])]});}
            var Q18;
            {var subQ0=sQuery(id+"F0.wireOp",EDGE,"E6");var subQ1=sQuery(id+"F0.wireOp",EDGE,"E0");var subQ2=makeQuery(id+"F0.imprint","INTERSECT",VERTEX,{"disambiguationData":[OD(0.0)],"derivedFrom":[subQ1,subQ0]});Q18=makeQuery(id+"F0.imprint","IMPRINT",FACE,{"disambiguationData":[TD([[makeQuery(id+"F0.imprint","IMPRINT",EDGE,{"disambiguationData":[TD([[subQ2,-1.0]])],"derivedFrom":subQ1}),1.0]])]});}
            var Q19;
            {var subQ0=sQuery(id+"F0.wireOp",EDGE,"E17");var subQ1=sQuery(id+"F0.wireOp",EDGE,"E0");var subQ2=makeQuery(id+"F0.imprint","INTERSECT",VERTEX,{"disambiguationData":[OD(0.0)],"derivedFrom":[subQ1,subQ0]});Q19=makeQuery(id+"F0.imprint","IMPRINT",FACE,{"disambiguationData":[TD([[makeQuery(id+"F0.imprint","IMPRINT",EDGE,{"disambiguationData":[TD([[subQ2,-1.0]])],"derivedFrom":subQ1}),1.0]])]});}
            extrude(context, id + "F4", {"entities" : qUnion([Q0, Q1, Q2, Q3, Q4, Q5, Q6, Q7, Q8, Q9, Q10, Q11, Q12, Q13, Q14, Q15, Q16, Q17, Q18, Q19]), "depth" : 3.8 * mm});
        }
        {
            var Q0;
            {var subQ0=sQuery(id+"F0.wireOp",EDGE,"E0");Q0=makeQuery(id+"F2.opExtrude","CAP_EDGE",EDGE,{"disambiguationData":[OSD([subQ0]),TDD([makeQuery(id+"F0.imprint","IMPRINT",EDGE,{"disambiguationData":[TD([[makeQuery(id+"F0.imprint","INTERSECT",VERTEX,{"disambiguationData":[OD(0.0)],"derivedFrom":[subQ0,sQuery(id+"F0.wireOp",EDGE,"E16")]}),1.0]])],"derivedFrom":subQ0})])],"isStart":false});}
            var Q1;
            {var subQ0=sQuery(id+"F0.wireOp",EDGE,"E0");Q1=makeQuery(id+"F4.opExtrude","CAP_EDGE",EDGE,{"disambiguationData":[OSD([subQ0]),TDD([makeQuery(id+"F0.imprint","IMPRINT",EDGE,{"disambiguationData":[TD([[makeQuery(id+"F0.imprint","INTERSECT",VERTEX,{"disambiguationData":[OD(1.0)],"derivedFrom":[subQ0,sQuery(id+"F0.wireOp",EDGE,"E7")]}),-1.0]])],"derivedFrom":subQ0})])],"isStart":false});}
            var Q2;
            {var subQ0=sQuery(id+"F0.wireOp",EDGE,"E0");var subQ1=makeQuery(id+"F0.imprint","INTERSECT",VERTEX,{"disambiguationData":[OD(0.0)],"derivedFrom":[subQ0,sQuery(id+"F0.wireOp",EDGE,"E17")]});var subQ2=sQuery(id+"F0.wireOp",EDGE,"E12");var subQ3=makeQuery(id+"F0.imprint","INTERSECT",VERTEX,{"disambiguationData":[OD(1.0)],"derivedFrom":[subQ0,sQuery(id+"F0.wireOp",EDGE,"E15")]});Q2=makeQuery(id+"F4.opExtrude","CAP_EDGE",EDGE,{"disambiguationData":[OSD([subQ0]),TDD([makeQuery(id+"F0.imprint","IMPRINT",EDGE,{"disambiguationData":[TD([[makeQuery(id+"F0.imprint","INTERSECT",VERTEX,{"disambiguationData":[OD(0.0)],"derivedFrom":[subQ0,subQ2]}),-1.0]])],"derivedFrom":subQ0}),makeQuery(id+"F0.imprint","IMPRINT",EDGE,{"disambiguationData":[TD([[subQ3,-1.0]])],"derivedFrom":subQ0}),makeQuery(id+"F0.imprint","IMPRINT",EDGE,{"disambiguationData":[TD([[subQ1,-1.0]])],"derivedFrom":subQ0})])],"isStart":false});}
            var Q3;
            {var subQ0=sQuery(id+"F0.wireOp",EDGE,"E0");Q3=makeQuery(id+"F4.opExtrude","CAP_EDGE",EDGE,{"disambiguationData":[OSD([subQ0]),TDD([makeQuery(id+"F0.imprint","IMPRINT",EDGE,{"disambiguationData":[TD([[makeQuery(id+"F0.imprint","INTERSECT",VERTEX,{"disambiguationData":[OD(0.0)],"derivedFrom":[subQ0,sQuery(id+"F0.wireOp",EDGE,"E15")]}),-1.0]])],"derivedFrom":subQ0})])],"isStart":false});}
            var Q4;
            {var subQ0=sQuery(id+"F0.wireOp",EDGE,"E0");Q4=makeQuery(id+"F2.opExtrude","CAP_EDGE",EDGE,{"disambiguationData":[OSD([subQ0]),TDD([makeQuery(id+"F0.imprint","IMPRINT",EDGE,{"disambiguationData":[TD([[makeQuery(id+"F0.imprint","INTERSECT",VERTEX,{"disambiguationData":[OD(1.0)],"derivedFrom":[subQ0,sQuery(id+"F0.wireOp",EDGE,"E14")]}),-1.0]])],"derivedFrom":subQ0})])],"isStart":false});}
            var Q5;
            {var subQ0=sQuery(id+"F0.wireOp",EDGE,"E0");Q5=makeQuery(id+"F4.opExtrude","CAP_EDGE",EDGE,{"disambiguationData":[OSD([subQ0]),TDD([makeQuery(id+"F0.imprint","IMPRINT",EDGE,{"disambiguationData":[TD([[makeQuery(id+"F0.imprint","INTERSECT",VERTEX,{"disambiguationData":[OD(0.0)],"derivedFrom":[subQ0,sQuery(id+"F0.wireOp",EDGE,"E9")]}),-1.0]])],"derivedFrom":subQ0})])],"isStart":false});}
            var Q6;
            {var subQ0=sQuery(id+"F0.wireOp",EDGE,"E0");var subQ1=makeQuery(id+"F0.imprint","INTERSECT",VERTEX,{"disambiguationData":[OD(0.0)],"derivedFrom":[subQ0,sQuery(id+"F0.wireOp",EDGE,"E14")]});var subQ2=sQuery(id+"F0.wireOp",EDGE,"E13");var subQ3=makeQuery(id+"F0.imprint","INTERSECT",VERTEX,{"disambiguationData":[OD(1.0)],"derivedFrom":[subQ0,sQuery(id+"F0.wireOp",EDGE,"E18")]});Q6=makeQuery(id+"F4.opExtrude","CAP_EDGE",EDGE,{"disambiguationData":[OSD([subQ0]),TDD([makeQuery(id+"F0.imprint","IMPRINT",EDGE,{"disambiguationData":[TD([[makeQuery(id+"F0.imprint","INTERSECT",VERTEX,{"disambiguationData":[OD(0.0)],"derivedFrom":[subQ0,subQ2]}),-1.0]])],"derivedFrom":subQ0}),makeQuery(id+"F0.imprint","IMPRINT",EDGE,{"disambiguationData":[TD([[subQ3,-1.0]])],"derivedFrom":subQ0}),makeQuery(id+"F0.imprint","IMPRINT",EDGE,{"disambiguationData":[TD([[subQ1,-1.0]])],"derivedFrom":subQ0})])],"isStart":false});}
            var Q7;
            {var subQ0=sQuery(id+"F0.wireOp",EDGE,"E0");Q7=makeQuery(id+"F4.opExtrude","CAP_EDGE",EDGE,{"disambiguationData":[OSD([subQ0]),TDD([makeQuery(id+"F0.imprint","IMPRINT",EDGE,{"disambiguationData":[TD([[makeQuery(id+"F0.imprint","INTERSECT",VERTEX,{"disambiguationData":[OD(0.0)],"derivedFrom":[subQ0,sQuery(id+"F0.wireOp",EDGE,"E18")]}),-1.0]])],"derivedFrom":subQ0})])],"isStart":false});}
            var Q8;
            {var subQ0=sQuery(id+"F0.wireOp",EDGE,"E0");Q8=makeQuery(id+"F2.opExtrude","CAP_EDGE",EDGE,{"disambiguationData":[OSD([subQ0]),TDD([makeQuery(id+"F0.imprint","IMPRINT",EDGE,{"disambiguationData":[TD([[makeQuery(id+"F0.imprint","INTERSECT",VERTEX,{"disambiguationData":[OD(1.0)],"derivedFrom":[subQ0,sQuery(id+"F0.wireOp",EDGE,"E20")]}),-1.0]])],"derivedFrom":subQ0})])],"isStart":false});}
            var Q9;
            {var subQ0=sQuery(id+"F0.wireOp",EDGE,"E0");Q9=makeQuery(id+"F4.opExtrude","CAP_EDGE",EDGE,{"disambiguationData":[OSD([subQ0]),TDD([makeQuery(id+"F0.imprint","IMPRINT",EDGE,{"disambiguationData":[TD([[makeQuery(id+"F0.imprint","INTERSECT",VERTEX,{"disambiguationData":[OD(0.0)],"derivedFrom":[subQ0,sQuery(id+"F0.wireOp",EDGE,"E6")]}),-1.0]])],"derivedFrom":subQ0})])],"isStart":false});}
            var Q10;
            {var subQ0=sQuery(id+"F0.wireOp",EDGE,"E0");var subQ1=makeQuery(id+"F0.imprint","INTERSECT",VERTEX,{"disambiguationData":[OD(0.0)],"derivedFrom":[subQ0,sQuery(id+"F0.wireOp",EDGE,"E20")]});var subQ2=sQuery(id+"F0.wireOp",EDGE,"E10");var subQ3=makeQuery(id+"F0.imprint","INTERSECT",VERTEX,{"disambiguationData":[OD(1.0)],"derivedFrom":[subQ0,sQuery(id+"F0.wireOp",EDGE,"E21")]});Q10=makeQuery(id+"F4.opExtrude","CAP_EDGE",EDGE,{"disambiguationData":[OSD([subQ0]),TDD([makeQuery(id+"F0.imprint","IMPRINT",EDGE,{"disambiguationData":[TD([[makeQuery(id+"F0.imprint","INTERSECT",VERTEX,{"disambiguationData":[OD(0.0)],"derivedFrom":[subQ0,subQ2]}),-1.0]])],"derivedFrom":subQ0}),makeQuery(id+"F0.imprint","IMPRINT",EDGE,{"disambiguationData":[TD([[subQ3,-1.0]])],"derivedFrom":subQ0}),makeQuery(id+"F0.imprint","IMPRINT",EDGE,{"disambiguationData":[TD([[subQ1,-1.0]])],"derivedFrom":subQ0})])],"isStart":false});}
            var Q11;
            {var subQ0=sQuery(id+"F0.wireOp",EDGE,"E0");Q11=makeQuery(id+"F4.opExtrude","CAP_EDGE",EDGE,{"disambiguationData":[OSD([subQ0]),TDD([makeQuery(id+"F0.imprint","IMPRINT",EDGE,{"disambiguationData":[TD([[makeQuery(id+"F0.imprint","INTERSECT",VERTEX,{"disambiguationData":[OD(0.0)],"derivedFrom":[subQ0,sQuery(id+"F0.wireOp",EDGE,"E21")]}),-1.0]])],"derivedFrom":subQ0})])],"isStart":false});}
            var Q12;
            {var subQ0=sQuery(id+"F0.wireOp",EDGE,"E0");Q12=makeQuery(id+"F2.opExtrude","CAP_EDGE",EDGE,{"disambiguationData":[OSD([subQ0]),TDD([makeQuery(id+"F0.imprint","IMPRINT",EDGE,{"disambiguationData":[TD([[makeQuery(id+"F0.imprint","INTERSECT",VERTEX,{"disambiguationData":[OD(1.0)],"derivedFrom":[subQ0,sQuery(id+"F0.wireOp",EDGE,"E19")]}),-1.0]])],"derivedFrom":subQ0})])],"isStart":false});}
            var Q13;
            {var subQ0=sQuery(id+"F0.wireOp",EDGE,"E0");Q13=makeQuery(id+"F4.opExtrude","CAP_EDGE",EDGE,{"disambiguationData":[OSD([subQ0]),TDD([makeQuery(id+"F0.imprint","IMPRINT",EDGE,{"disambiguationData":[TD([[makeQuery(id+"F0.imprint","INTERSECT",VERTEX,{"disambiguationData":[OD(0.0)],"derivedFrom":[subQ0,sQuery(id+"F0.wireOp",EDGE,"E8")]}),-1.0]])],"derivedFrom":subQ0})])],"isStart":false});}
            var Q14;
            {var subQ0=sQuery(id+"F0.wireOp",EDGE,"E0");var subQ1=makeQuery(id+"F0.imprint","INTERSECT",VERTEX,{"disambiguationData":[OD(0.0)],"derivedFrom":[subQ0,sQuery(id+"F0.wireOp",EDGE,"E19")]});var subQ2=sQuery(id+"F0.wireOp",EDGE,"E11");var subQ3=makeQuery(id+"F0.imprint","INTERSECT",VERTEX,{"disambiguationData":[OD(1.0)],"derivedFrom":[subQ0,sQuery(id+"F0.wireOp",EDGE,"E16")]});Q14=makeQuery(id+"F4.opExtrude","CAP_EDGE",EDGE,{"disambiguationData":[OSD([subQ0]),TDD([makeQuery(id+"F0.imprint","IMPRINT",EDGE,{"disambiguationData":[TD([[makeQuery(id+"F0.imprint","INTERSECT",VERTEX,{"disambiguationData":[OD(0.0)],"derivedFrom":[subQ0,subQ2]}),-1.0]])],"derivedFrom":subQ0}),makeQuery(id+"F0.imprint","IMPRINT",EDGE,{"disambiguationData":[TD([[subQ3,-1.0]])],"derivedFrom":subQ0}),makeQuery(id+"F0.imprint","IMPRINT",EDGE,{"disambiguationData":[TD([[subQ1,-1.0]])],"derivedFrom":subQ0})])],"isStart":false});}
            var Q15;
            {var subQ0=sQuery(id+"F0.wireOp",EDGE,"E0");Q15=makeQuery(id+"F4.opExtrude","CAP_EDGE",EDGE,{"disambiguationData":[OSD([subQ0]),TDD([makeQuery(id+"F0.imprint","IMPRINT",EDGE,{"disambiguationData":[TD([[makeQuery(id+"F0.imprint","INTERSECT",VERTEX,{"disambiguationData":[OD(0.0)],"derivedFrom":[subQ0,sQuery(id+"F0.wireOp",EDGE,"E7")]}),1.0]])],"derivedFrom":subQ0})])],"isStart":false});}
            fillet(context, id + "F5", {"entities" : qUnion([Q0, Q1, Q2, Q3, Q4, Q5, Q6, Q7, Q8, Q9, Q10, Q11, Q12, Q13, Q14, Q15]), "radius" : 1.27 * mm, "tangentPropagation" : true, "allowEdgeOverflow" : false});
        }
    });
